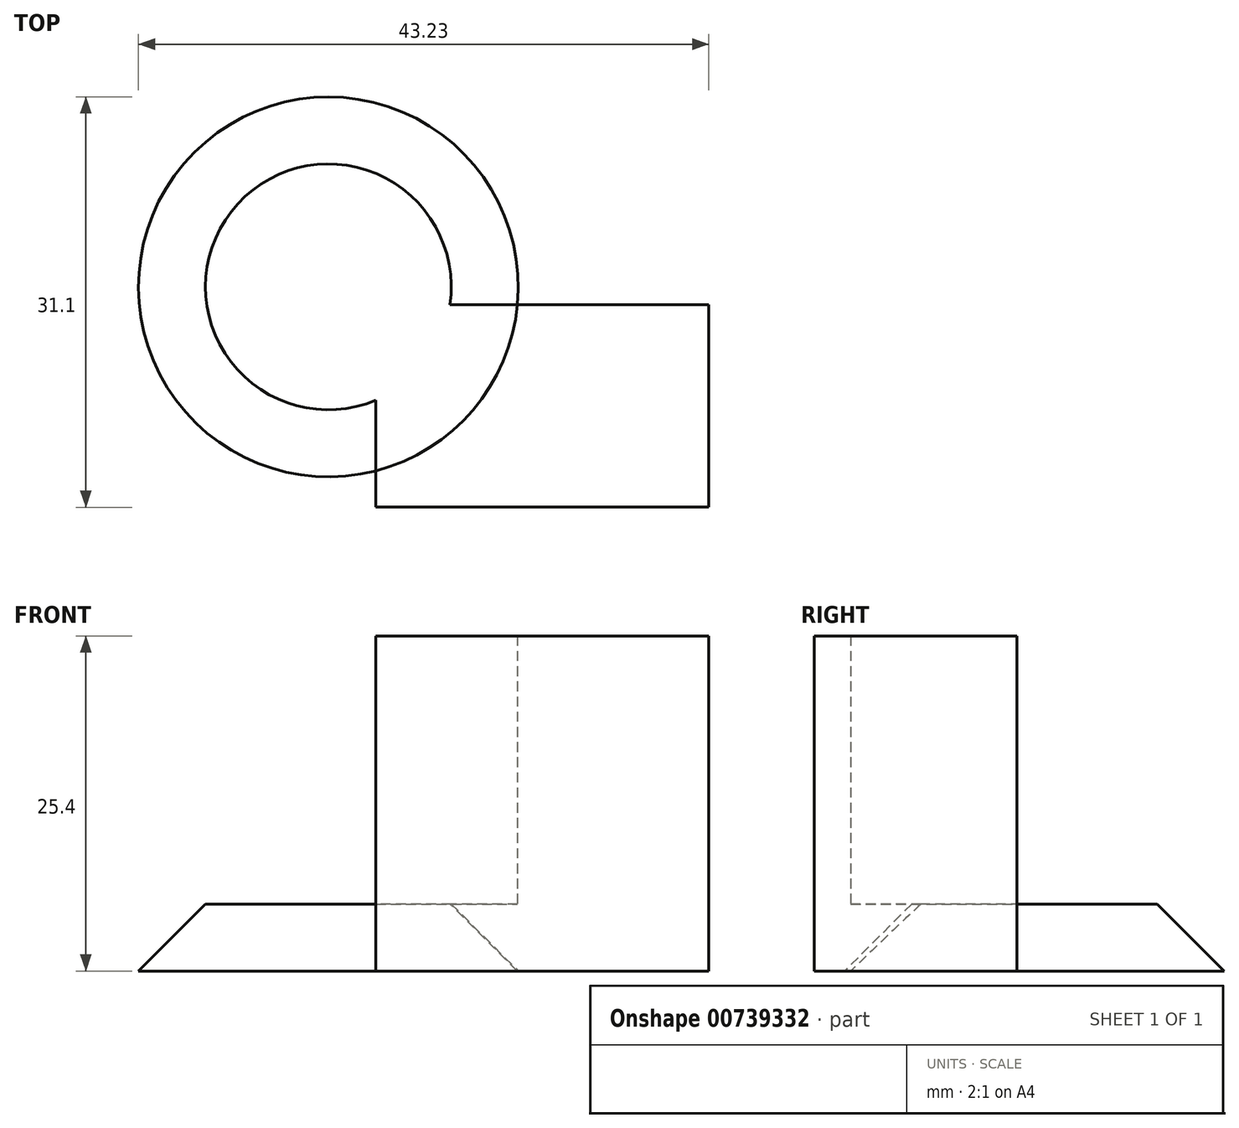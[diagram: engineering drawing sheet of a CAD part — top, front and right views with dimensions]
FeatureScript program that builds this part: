
annotation { "Feature Type Name" : "Feature", "Feature Type Description" : "" }
export const myFeature = defineFeature(function(context is Context, id is Id, definition is map)
    precondition{}
    {
        {
            var Q0;
            Q0=qCreatedBy(makeId("Top.planeOp"),FACE);
            var sketch = newSketch(context, id + "F0", { "sketchPlane" : qUnion([Q0])});
            skLineSegment(sketch, "E0.bottom", {"start": v(-54, 23.09) * mm, "end": v(-28.76, 23.09) * mm});
            skLineSegment(sketch, "E0.top", {"start": v(-54, 7.73) * mm, "end": v(-28.76, 7.73) * mm});
            skLineSegment(sketch, "E0.left", {"start": v(-54, 23.09) * mm, "end": v(-54, 7.73) * mm});
            skLineSegment(sketch, "E0.right", {"start": v(-28.76, 23.09) * mm, "end": v(-28.76, 7.73) * mm});
            skCircle(sketch, "E1", {"center": v(-57.6, 24.43) * mm, "radius": 14.4 * mm});
            skSolve(sketch);
        }
        {
            var Q0;
            {var subQ2=sQuery(id+"F0.wireOp",EDGE,"E0.top");Q0=makeQuery(id+"F0.imprint","IMPRINT",FACE,{"disambiguationData":[TD([[makeQuery(id+"F0.imprint","IMPRINT",EDGE,{"derivedFrom":subQ2}),1.0]])]});}
            extrude(context, id + "F1", {"entities" : qUnion([Q0]), "depth" : 25.4 * mm, "offsetDistance" : 25.4 * mm});
        }
        {
            var Q0;
            {var subQ0=sQuery(id+"F0.wireOp",EDGE,"E0.left");var subQ1=sQuery(id+"F0.wireOp",EDGE,"E0.bottom");var subQ2=makeQuery(id+"F0.imprint","INTERSECT",VERTEX,{"derivedFrom":[subQ1,subQ0]});Q0=makeQuery(id+"F0.imprint","IMPRINT",FACE,{"disambiguationData":[TD([[makeQuery(id+"F0.imprint","IMPRINT",EDGE,{"disambiguationData":[TD([[subQ2,-1.0]])],"derivedFrom":subQ1}),1.0]])]});}
            var Q1;
            {var subQ0=sQuery(id+"F0.wireOp",EDGE,"E0.left");var subQ1=sQuery(id+"F0.wireOp",EDGE,"E0.bottom");var subQ2=makeQuery(id+"F0.imprint","INTERSECT",VERTEX,{"derivedFrom":[subQ1,subQ0]});Q1=makeQuery(id+"F0.imprint","IMPRINT",FACE,{"disambiguationData":[TD([[makeQuery(id+"F0.imprint","IMPRINT",EDGE,{"disambiguationData":[TD([[subQ2,-1.0]])],"derivedFrom":subQ1}),-1.0]])]});}
            extrude(context, id + "F2", {"entities" : qUnion([Q0, Q1]), "operationType" : NewBodyOperationType.ADD, "depth" : 5.08 * mm, "offsetDistance" : 25.4 * mm});
        }
        {
            var Q0;
            {var subQ0=sQuery(id+"F0.wireOp",EDGE,"E1");Q0=makeQuery(id+"F2.boolean.opBoolean","SPLIT",EDGE,{"disambiguationData":[topologyDisambiguationEdgeConnected([makeQuery(id+"F1.opExtrude","SWEPT_FACE",FACE,{"disambiguationData":[OSD([subQ0])]})])],"derivedFrom":makeQuery(id+"F2.opExtrude","CAP_EDGE",EDGE,{"disambiguationData":[OSD([subQ0])],"isStart":false})});}
            chamfer(context, id + "F3", {"entities" : qUnion([Q0]), "width" : 5.08 * mm, "tangentPropagation" : true});
        }
    });
